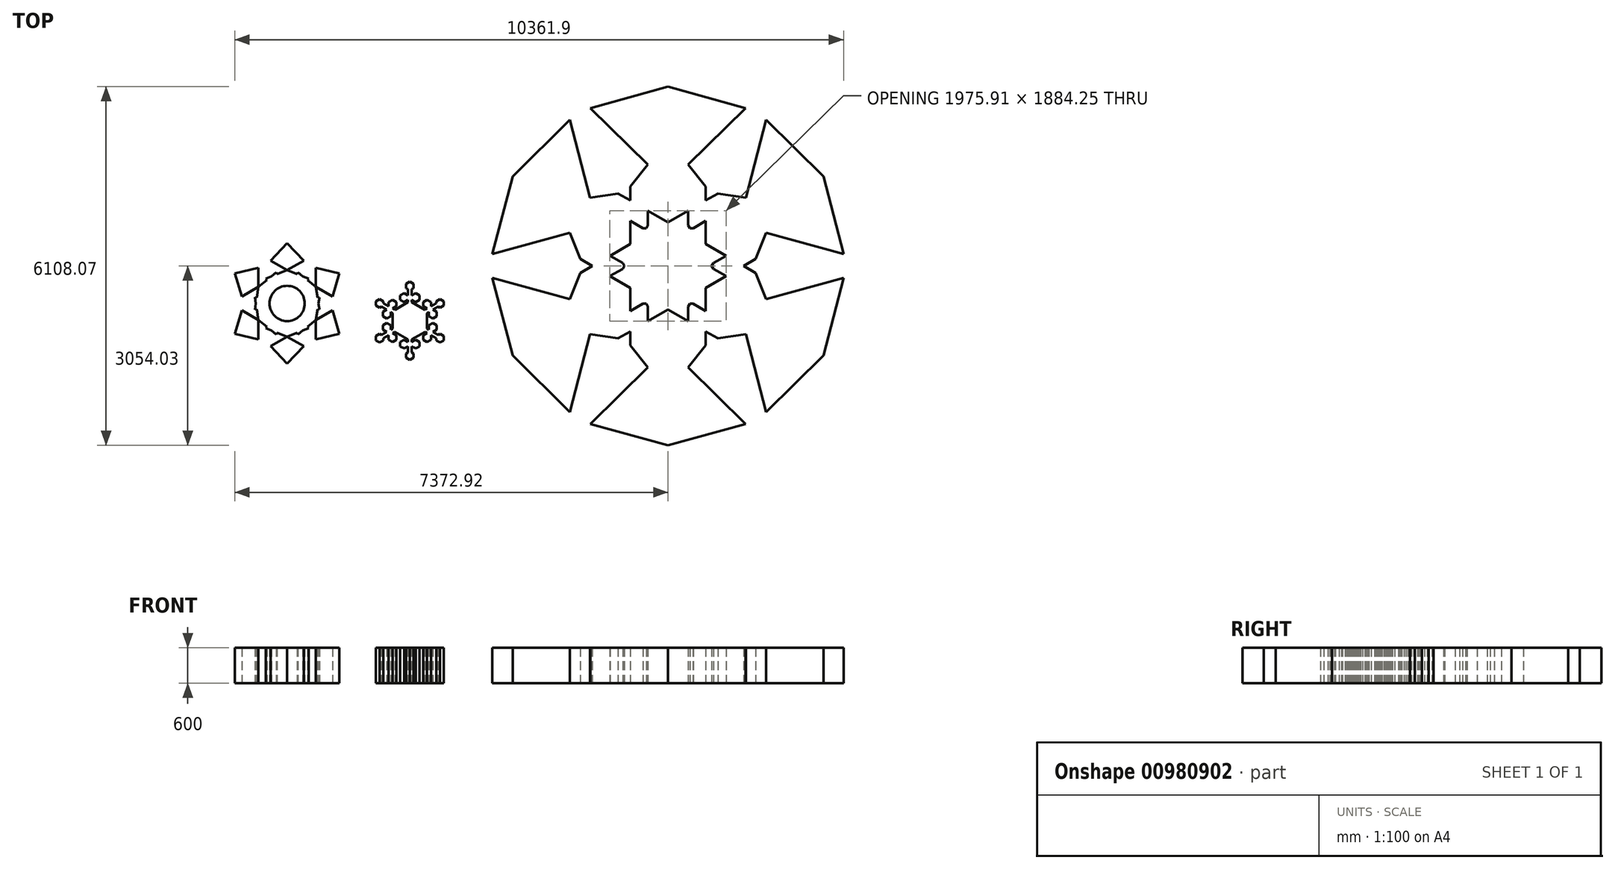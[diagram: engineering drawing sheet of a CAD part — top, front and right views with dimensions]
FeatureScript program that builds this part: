
annotation { "Feature Type Name" : "Feature", "Feature Type Description" : "" }
export const myFeature = defineFeature(function(context is Context, id is Id, definition is map)
    precondition{}
    {
        {
            var Q0;
            Q0=qCreatedBy(makeId("Top.planeOp"),FACE);
            var sketch = newSketch(context, id + "F0", { "sketchPlane" : qUnion([Q0])});
            skLineSegment(sketch, "E0", {"start": v(525.43, 83.54) * mm, "end": v(525.43, -246.83) * mm});
            skCircle(sketch, "E1.cCircle", {"center": v(525.43, 251.11) * mm, "radius": 145.12 * mm, "construction": true});
            skLineSegment(sketch, "E1.0", {"start": v(670.55, 167.33) * mm, "end": v(525.43, 83.54) * mm});
            skLineSegment(sketch, "E1.1", {"start": v(525.43, 83.54) * mm, "end": v(380.31, 167.33) * mm});
            skLineSegment(sketch, "E1.2", {"start": v(380.31, 167.33) * mm, "end": v(380.31, 334.9) * mm});
            skLineSegment(sketch, "E1.3", {"start": v(380.31, 334.9) * mm, "end": v(525.43, 418.68) * mm});
            skLineSegment(sketch, "E1.4", {"start": v(525.43, 418.68) * mm, "end": v(670.55, 334.9) * mm});
            skLineSegment(sketch, "E1.5", {"start": v(670.55, 334.9) * mm, "end": v(670.55, 167.33) * mm});
            skPoint(sketch, "E1.0.midPoint", {"position": v(598, 125.43) * mm});
            skCircle(sketch, "E2.cCircle", {"center": v(525.43, -173.92) * mm, "radius": 63.14 * mm, "construction": true});
            skLineSegment(sketch, "E2.0", {"start": v(525.43, -246.83) * mm, "end": v(462.3, -210.38) * mm});
            skLineSegment(sketch, "E2.1", {"start": v(462.3, -210.38) * mm, "end": v(462.3, -137.47) * mm});
            skLineSegment(sketch, "E2.2", {"start": v(462.3, -137.47) * mm, "end": v(525.43, -101.01) * mm});
            skLineSegment(sketch, "E2.3", {"start": v(525.43, -101.01) * mm, "end": v(588.57, -137.47) * mm});
            skLineSegment(sketch, "E2.4", {"start": v(588.57, -137.47) * mm, "end": v(588.57, -210.38) * mm});
            skLineSegment(sketch, "E2.5", {"start": v(588.57, -210.38) * mm, "end": v(525.43, -246.83) * mm});
            skPoint(sketch, "E2.0.midPoint", {"position": v(493.86, -228.6) * mm});
            skLineSegment(sketch, "E3", {"start": v(492.43, 102.6) * mm, "end": v(492.43, -120.07) * mm});
            skLineSegment(sketch, "E4.MirrorCS", {"start": v(558.43, 102.6) * mm, "end": v(558.43, -120.07) * mm});
            skCircle(sketch, "E5.cCircle", {"center": v(426.9, 22.57) * mm, "radius": 65.53 * mm, "construction": true});
            skLineSegment(sketch, "E5.0", {"start": v(492.43, -15.27) * mm, "end": v(426.9, -53.1) * mm});
            skLineSegment(sketch, "E5.1", {"start": v(426.9, -53.1) * mm, "end": v(361.36, -15.27) * mm});
            skLineSegment(sketch, "E5.2", {"start": v(361.36, -15.27) * mm, "end": v(361.36, 60.4) * mm});
            skLineSegment(sketch, "E5.3", {"start": v(361.36, 60.4) * mm, "end": v(426.9, 98.24) * mm});
            skLineSegment(sketch, "E5.4", {"start": v(426.9, 98.24) * mm, "end": v(492.43, 60.4) * mm});
            skLineSegment(sketch, "E5.5", {"start": v(492.43, 60.4) * mm, "end": v(492.43, -15.27) * mm});
            skPoint(sketch, "E5.0.midPoint", {"position": v(459.67, -34.18) * mm});
            skLineSegment(sketch, "E6.MirrorCS", {"start": v(689.5, -15.27) * mm, "end": v(689.5, 60.4) * mm});
            skLineSegment(sketch, "E7.MirrorCS", {"start": v(689.5, 60.4) * mm, "end": v(623.97, 98.24) * mm});
            skLineSegment(sketch, "E8.MirrorCS", {"start": v(623.97, 98.24) * mm, "end": v(558.43, 60.4) * mm});
            skLineSegment(sketch, "E9.MirrorCS", {"start": v(558.43, -15.27) * mm, "end": v(623.97, -53.1) * mm});
            skLineSegment(sketch, "E10.MirrorCS", {"start": v(623.97, -53.1) * mm, "end": v(689.5, -15.27) * mm});
            skLineSegment(sketch, "E11.1.0", {"start": v(815.68, 251.11) * mm, "end": v(1101.79, 85.92) * mm});
            skLineSegment(sketch, "E11.1.1", {"start": v(815.68, 289.22) * mm, "end": v(1008.5, 177.89) * mm});
            skLineSegment(sketch, "E11.1.2", {"start": v(815.68, 418.68) * mm, "end": v(815.68, 251.11) * mm});
            skLineSegment(sketch, "E11.1.3", {"start": v(525.43, 418.68) * mm, "end": v(670.55, 502.47) * mm});
            skCircle(sketch, "E11.1.4", {"center": v(670.55, 334.9) * mm, "radius": 145.12 * mm, "construction": true});
            skLineSegment(sketch, "E11.1.5", {"start": v(917.74, 230.29) * mm, "end": v(983.28, 268.12) * mm});
            skPoint(sketch, "E11.1.6", {"position": v(815.68, 334.9) * mm});
            skLineSegment(sketch, "E11.1.7", {"start": v(983.28, 343.8) * mm, "end": v(917.74, 381.63) * mm});
            skLineSegment(sketch, "E11.1.8", {"start": v(917.74, 381.63) * mm, "end": v(852.2, 343.8) * mm});
            skLineSegment(sketch, "E11.1.9", {"start": v(670.55, 167.33) * mm, "end": v(525.43, 251.11) * mm});
            skPoint(sketch, "E11.1.10", {"position": v(884.74, 135.3) * mm});
            skLineSegment(sketch, "E11.1.11", {"start": v(815.68, 251.11) * mm, "end": v(670.55, 167.33) * mm});
            skCircle(sketch, "E11.1.12", {"center": v(1038.65, 122.38) * mm, "radius": 63.14 * mm, "construction": true});
            skLineSegment(sketch, "E11.1.13", {"start": v(983.28, 268.12) * mm, "end": v(983.28, 343.8) * mm});
            skLineSegment(sketch, "E11.1.14", {"start": v(670.55, 502.47) * mm, "end": v(815.68, 418.68) * mm});
            skCircle(sketch, "E11.1.15", {"center": v(819.2, 135.3) * mm, "radius": 65.53 * mm, "construction": true});
            skPoint(sketch, "E11.1.16", {"position": v(1070.22, 67.7) * mm});
            skLineSegment(sketch, "E11.1.17", {"start": v(525.43, 251.11) * mm, "end": v(525.43, 418.68) * mm});
            skLineSegment(sketch, "E11.1.18", {"start": v(782.68, 232.06) * mm, "end": v(975.5, 120.73) * mm});
            skLineSegment(sketch, "E11.1.19", {"start": v(852.2, 343.8) * mm, "end": v(852.2, 268.12) * mm});
            skLineSegment(sketch, "E11.1.20", {"start": v(1038.65, 195.3) * mm, "end": v(1101.79, 158.84) * mm});
            skLineSegment(sketch, "E11.1.21", {"start": v(819.2, 210.97) * mm, "end": v(884.74, 173.13) * mm});
            skLineSegment(sketch, "E11.1.22", {"start": v(1038.65, 49.47) * mm, "end": v(975.5, 85.92) * mm});
            skLineSegment(sketch, "E11.1.23", {"start": v(1101.79, 158.84) * mm, "end": v(1101.79, 85.92) * mm});
            skLineSegment(sketch, "E11.1.24", {"start": v(975.5, 85.92) * mm, "end": v(975.5, 158.84) * mm});
            skLineSegment(sketch, "E11.1.25", {"start": v(884.74, 97.46) * mm, "end": v(819.2, 59.62) * mm});
            skLineSegment(sketch, "E11.1.26", {"start": v(975.5, 158.84) * mm, "end": v(1038.65, 195.3) * mm});
            skLineSegment(sketch, "E11.1.27", {"start": v(753.67, 173.13) * mm, "end": v(819.2, 210.97) * mm});
            skLineSegment(sketch, "E11.1.28", {"start": v(884.74, 173.13) * mm, "end": v(884.74, 97.46) * mm});
            skLineSegment(sketch, "E11.1.29", {"start": v(1101.79, 85.92) * mm, "end": v(1038.65, 49.47) * mm});
            skLineSegment(sketch, "E11.1.30", {"start": v(753.67, 97.46) * mm, "end": v(753.67, 173.13) * mm});
            skLineSegment(sketch, "E11.1.31", {"start": v(819.2, 59.62) * mm, "end": v(753.67, 97.46) * mm});
            skLineSegment(sketch, "E11.2.0", {"start": v(815.68, 586.26) * mm, "end": v(1101.79, 751.44) * mm});
            skLineSegment(sketch, "E11.2.1", {"start": v(782.68, 605.3) * mm, "end": v(975.5, 716.64) * mm});
            skLineSegment(sketch, "E11.2.2", {"start": v(670.55, 670.04) * mm, "end": v(815.68, 586.26) * mm});
            skLineSegment(sketch, "E11.2.3", {"start": v(525.43, 418.68) * mm, "end": v(525.43, 586.26) * mm});
            skCircle(sketch, "E11.2.4", {"center": v(670.55, 502.47) * mm, "radius": 145.12 * mm, "construction": true});
            skLineSegment(sketch, "E11.2.5", {"start": v(884.74, 664.24) * mm, "end": v(884.74, 739.9) * mm});
            skPoint(sketch, "E11.2.6", {"position": v(743.11, 628.15) * mm});
            skLineSegment(sketch, "E11.2.7", {"start": v(819.2, 777.75) * mm, "end": v(753.67, 739.9) * mm});
            skLineSegment(sketch, "E11.2.8", {"start": v(753.67, 739.9) * mm, "end": v(753.67, 664.24) * mm});
            skLineSegment(sketch, "E11.2.9", {"start": v(815.68, 418.68) * mm, "end": v(670.55, 334.9) * mm});
            skPoint(sketch, "E11.2.10", {"position": v(950.51, 588.16) * mm});
            skLineSegment(sketch, "E11.2.11", {"start": v(815.68, 586.26) * mm, "end": v(815.68, 418.68) * mm});
            skCircle(sketch, "E11.2.12", {"center": v(1038.65, 714.99) * mm, "radius": 63.14 * mm, "construction": true});
            skLineSegment(sketch, "E11.2.13", {"start": v(884.74, 739.9) * mm, "end": v(819.2, 777.75) * mm});
            skLineSegment(sketch, "E11.2.14", {"start": v(525.43, 586.26) * mm, "end": v(670.55, 670.04) * mm});
            skCircle(sketch, "E11.2.15", {"center": v(917.74, 531.4) * mm, "radius": 65.53 * mm, "construction": true});
            skPoint(sketch, "E11.2.16", {"position": v(1101.79, 714.99) * mm});
            skLineSegment(sketch, "E11.2.17", {"start": v(670.55, 334.9) * mm, "end": v(525.43, 418.68) * mm});
            skLineSegment(sketch, "E11.2.18", {"start": v(815.68, 548.15) * mm, "end": v(1008.5, 659.48) * mm});
            skLineSegment(sketch, "E11.2.19", {"start": v(753.67, 664.24) * mm, "end": v(819.2, 626.4) * mm});
            skLineSegment(sketch, "E11.2.20", {"start": v(975.5, 751.44) * mm, "end": v(1038.65, 787.9) * mm});
            skLineSegment(sketch, "E11.2.21", {"start": v(852.2, 569.24) * mm, "end": v(917.74, 607.08) * mm});
            skLineSegment(sketch, "E11.2.22", {"start": v(1101.79, 678.53) * mm, "end": v(1038.65, 642.08) * mm});
            skLineSegment(sketch, "E11.2.23", {"start": v(1038.65, 787.9) * mm, "end": v(1101.79, 751.44) * mm});
            skLineSegment(sketch, "E11.2.24", {"start": v(1038.65, 642.08) * mm, "end": v(975.5, 678.53) * mm});
            skLineSegment(sketch, "E11.2.25", {"start": v(983.28, 569.24) * mm, "end": v(983.28, 493.57) * mm});
            skLineSegment(sketch, "E11.2.26", {"start": v(975.5, 678.53) * mm, "end": v(975.5, 751.44) * mm});
            skLineSegment(sketch, "E11.2.27", {"start": v(852.2, 493.57) * mm, "end": v(852.2, 569.24) * mm});
            skLineSegment(sketch, "E11.2.28", {"start": v(917.74, 607.08) * mm, "end": v(983.28, 569.24) * mm});
            skLineSegment(sketch, "E11.2.29", {"start": v(1101.79, 751.44) * mm, "end": v(1101.79, 678.53) * mm});
            skLineSegment(sketch, "E11.2.30", {"start": v(917.74, 455.73) * mm, "end": v(852.2, 493.57) * mm});
            skLineSegment(sketch, "E11.2.31", {"start": v(983.28, 493.57) * mm, "end": v(917.74, 455.73) * mm});
            skLineSegment(sketch, "E11.3.0", {"start": v(525.43, 753.83) * mm, "end": v(525.43, 1084.2) * mm});
            skLineSegment(sketch, "E11.3.1", {"start": v(492.43, 734.78) * mm, "end": v(492.43, 957.43) * mm});
            skLineSegment(sketch, "E11.3.2", {"start": v(380.31, 670.04) * mm, "end": v(525.43, 753.83) * mm});
            skLineSegment(sketch, "E11.3.3", {"start": v(525.43, 418.68) * mm, "end": v(380.31, 502.47) * mm});
            skCircle(sketch, "E11.3.4", {"center": v(525.43, 586.26) * mm, "radius": 145.12 * mm, "construction": true});
            skLineSegment(sketch, "E11.3.5", {"start": v(492.43, 852.63) * mm, "end": v(426.9, 890.47) * mm});
            skPoint(sketch, "E11.3.6", {"position": v(452.87, 711.93) * mm});
            skLineSegment(sketch, "E11.3.7", {"start": v(361.36, 852.63) * mm, "end": v(361.36, 776.96) * mm});
            skLineSegment(sketch, "E11.3.8", {"start": v(361.36, 776.96) * mm, "end": v(426.9, 739.12) * mm});
            skLineSegment(sketch, "E11.3.9", {"start": v(670.55, 670.04) * mm, "end": v(670.55, 502.47) * mm});
            skPoint(sketch, "E11.3.10", {"position": v(591.2, 871.55) * mm});
            skLineSegment(sketch, "E11.3.11", {"start": v(525.43, 753.83) * mm, "end": v(670.55, 670.04) * mm});
            skCircle(sketch, "E11.3.12", {"center": v(525.43, 1011.3) * mm, "radius": 63.14 * mm, "construction": true});
            skLineSegment(sketch, "E11.3.13", {"start": v(426.9, 890.47) * mm, "end": v(361.36, 852.63) * mm});
            skLineSegment(sketch, "E11.3.14", {"start": v(380.31, 502.47) * mm, "end": v(380.31, 670.04) * mm});
            skCircle(sketch, "E11.3.15", {"center": v(623.97, 814.8) * mm, "radius": 65.53 * mm, "construction": true});
            skPoint(sketch, "E11.3.16", {"position": v(557, 1065.97) * mm});
            skLineSegment(sketch, "E11.3.17", {"start": v(670.55, 502.47) * mm, "end": v(525.43, 418.68) * mm});
            skLineSegment(sketch, "E11.3.18", {"start": v(558.43, 734.78) * mm, "end": v(558.43, 957.43) * mm});
            skLineSegment(sketch, "E11.3.19", {"start": v(426.9, 739.12) * mm, "end": v(492.43, 776.96) * mm});
            skLineSegment(sketch, "E11.3.20", {"start": v(462.3, 974.84) * mm, "end": v(462.3, 1047.75) * mm});
            skLineSegment(sketch, "E11.3.21", {"start": v(558.43, 776.96) * mm, "end": v(558.43, 852.63) * mm});
            skLineSegment(sketch, "E11.3.22", {"start": v(588.57, 1047.75) * mm, "end": v(588.57, 974.84) * mm});
            skLineSegment(sketch, "E11.3.23", {"start": v(462.3, 1047.75) * mm, "end": v(525.43, 1084.2) * mm});
            skLineSegment(sketch, "E11.3.24", {"start": v(588.57, 974.84) * mm, "end": v(525.43, 938.38) * mm});
            skLineSegment(sketch, "E11.3.25", {"start": v(623.97, 890.47) * mm, "end": v(689.5, 852.63) * mm});
            skLineSegment(sketch, "E11.3.26", {"start": v(525.43, 938.38) * mm, "end": v(462.3, 974.84) * mm});
            skLineSegment(sketch, "E11.3.27", {"start": v(623.97, 739.12) * mm, "end": v(558.43, 776.96) * mm});
            skLineSegment(sketch, "E11.3.28", {"start": v(558.43, 852.63) * mm, "end": v(623.97, 890.47) * mm});
            skLineSegment(sketch, "E11.3.29", {"start": v(525.43, 1084.2) * mm, "end": v(588.57, 1047.75) * mm});
            skLineSegment(sketch, "E11.3.30", {"start": v(689.5, 776.96) * mm, "end": v(623.97, 739.12) * mm});
            skLineSegment(sketch, "E11.3.31", {"start": v(689.5, 852.63) * mm, "end": v(689.5, 776.96) * mm});
            skLineSegment(sketch, "E11.4.0", {"start": v(235.19, 586.26) * mm, "end": v(-50.92, 751.44) * mm});
            skLineSegment(sketch, "E11.4.1", {"start": v(235.19, 548.15) * mm, "end": v(42.36, 659.48) * mm});
            skLineSegment(sketch, "E11.4.2", {"start": v(235.19, 418.68) * mm, "end": v(235.19, 586.26) * mm});
            skLineSegment(sketch, "E11.4.3", {"start": v(525.43, 418.68) * mm, "end": v(380.31, 334.9) * mm});
            skCircle(sketch, "E11.4.4", {"center": v(380.31, 502.47) * mm, "radius": 145.12 * mm, "construction": true});
            skLineSegment(sketch, "E11.4.5", {"start": v(133.12, 607.08) * mm, "end": v(67.59, 569.24) * mm});
            skPoint(sketch, "E11.4.6", {"position": v(235.19, 502.47) * mm});
            skLineSegment(sketch, "E11.4.7", {"start": v(67.59, 493.57) * mm, "end": v(133.12, 455.73) * mm});
            skLineSegment(sketch, "E11.4.8", {"start": v(133.12, 455.73) * mm, "end": v(198.66, 493.57) * mm});
            skLineSegment(sketch, "E11.4.9", {"start": v(380.31, 670.04) * mm, "end": v(525.43, 586.26) * mm});
            skPoint(sketch, "E11.4.10", {"position": v(166.12, 702.07) * mm});
            skLineSegment(sketch, "E11.4.11", {"start": v(235.19, 586.26) * mm, "end": v(380.31, 670.04) * mm});
            skCircle(sketch, "E11.4.12", {"center": v(12.22, 714.99) * mm, "radius": 63.14 * mm, "construction": true});
            skLineSegment(sketch, "E11.4.13", {"start": v(67.59, 569.24) * mm, "end": v(67.59, 493.57) * mm});
            skLineSegment(sketch, "E11.4.14", {"start": v(380.31, 334.9) * mm, "end": v(235.19, 418.68) * mm});
            skCircle(sketch, "E11.4.15", {"center": v(231.66, 702.07) * mm, "radius": 65.53 * mm, "construction": true});
            skPoint(sketch, "E11.4.16", {"position": v(-19.35, 769.67) * mm});
            skLineSegment(sketch, "E11.4.17", {"start": v(525.43, 586.26) * mm, "end": v(525.43, 418.68) * mm});
            skLineSegment(sketch, "E11.4.18", {"start": v(268.19, 605.3) * mm, "end": v(75.36, 716.64) * mm});
            skLineSegment(sketch, "E11.4.19", {"start": v(198.66, 493.57) * mm, "end": v(198.66, 569.24) * mm});
            skLineSegment(sketch, "E11.4.20", {"start": v(12.22, 642.08) * mm, "end": v(-50.92, 678.53) * mm});
            skLineSegment(sketch, "E11.4.21", {"start": v(231.66, 626.4) * mm, "end": v(166.12, 664.24) * mm});
            skLineSegment(sketch, "E11.4.22", {"start": v(12.22, 787.9) * mm, "end": v(75.36, 751.44) * mm});
            skLineSegment(sketch, "E11.4.23", {"start": v(-50.92, 678.53) * mm, "end": v(-50.92, 751.44) * mm});
            skLineSegment(sketch, "E11.4.24", {"start": v(75.36, 751.44) * mm, "end": v(75.36, 678.53) * mm});
            skLineSegment(sketch, "E11.4.25", {"start": v(166.12, 739.9) * mm, "end": v(231.66, 777.75) * mm});
            skLineSegment(sketch, "E11.4.26", {"start": v(75.36, 678.53) * mm, "end": v(12.22, 642.08) * mm});
            skLineSegment(sketch, "E11.4.27", {"start": v(297.2, 664.24) * mm, "end": v(231.66, 626.4) * mm});
            skLineSegment(sketch, "E11.4.28", {"start": v(166.12, 664.24) * mm, "end": v(166.12, 739.9) * mm});
            skLineSegment(sketch, "E11.4.29", {"start": v(-50.92, 751.44) * mm, "end": v(12.22, 787.9) * mm});
            skLineSegment(sketch, "E11.4.30", {"start": v(297.2, 739.9) * mm, "end": v(297.2, 664.24) * mm});
            skLineSegment(sketch, "E11.4.31", {"start": v(231.66, 777.75) * mm, "end": v(297.2, 739.9) * mm});
            skLineSegment(sketch, "E11.5.0", {"start": v(235.19, 251.11) * mm, "end": v(-50.92, 85.92) * mm});
            skLineSegment(sketch, "E11.5.1", {"start": v(268.19, 232.06) * mm, "end": v(75.36, 120.73) * mm});
            skLineSegment(sketch, "E11.5.2", {"start": v(380.31, 167.33) * mm, "end": v(235.19, 251.11) * mm});
            skLineSegment(sketch, "E11.5.3", {"start": v(525.43, 418.68) * mm, "end": v(525.43, 251.11) * mm});
            skCircle(sketch, "E11.5.4", {"center": v(380.31, 334.9) * mm, "radius": 145.12 * mm, "construction": true});
            skLineSegment(sketch, "E11.5.5", {"start": v(166.12, 173.13) * mm, "end": v(166.12, 97.46) * mm});
            skPoint(sketch, "E11.5.6", {"position": v(307.75, 209.22) * mm});
            skLineSegment(sketch, "E11.5.7", {"start": v(231.66, 59.62) * mm, "end": v(297.2, 97.46) * mm});
            skLineSegment(sketch, "E11.5.8", {"start": v(297.2, 97.46) * mm, "end": v(297.2, 173.13) * mm});
            skLineSegment(sketch, "E11.5.9", {"start": v(235.19, 418.68) * mm, "end": v(380.31, 502.47) * mm});
            skPoint(sketch, "E11.5.10", {"position": v(100.35, 249.2) * mm});
            skLineSegment(sketch, "E11.5.11", {"start": v(235.19, 251.11) * mm, "end": v(235.19, 418.68) * mm});
            skCircle(sketch, "E11.5.12", {"center": v(12.22, 122.38) * mm, "radius": 63.14 * mm, "construction": true});
            skLineSegment(sketch, "E11.5.13", {"start": v(166.12, 97.46) * mm, "end": v(231.66, 59.62) * mm});
            skLineSegment(sketch, "E11.5.14", {"start": v(525.43, 251.11) * mm, "end": v(380.31, 167.33) * mm});
            skCircle(sketch, "E11.5.15", {"center": v(133.12, 305.96) * mm, "radius": 65.53 * mm, "construction": true});
            skPoint(sketch, "E11.5.16", {"position": v(-50.92, 122.38) * mm});
            skLineSegment(sketch, "E11.5.17", {"start": v(380.31, 502.47) * mm, "end": v(525.43, 418.68) * mm});
            skLineSegment(sketch, "E11.5.18", {"start": v(235.19, 289.22) * mm, "end": v(42.36, 177.89) * mm});
            skLineSegment(sketch, "E11.5.19", {"start": v(297.2, 173.13) * mm, "end": v(231.66, 210.97) * mm});
            skLineSegment(sketch, "E11.5.20", {"start": v(75.36, 85.92) * mm, "end": v(12.22, 49.47) * mm});
            skLineSegment(sketch, "E11.5.21", {"start": v(198.66, 268.12) * mm, "end": v(133.12, 230.29) * mm});
            skLineSegment(sketch, "E11.5.22", {"start": v(-50.92, 158.84) * mm, "end": v(12.22, 195.3) * mm});
            skLineSegment(sketch, "E11.5.23", {"start": v(12.22, 49.47) * mm, "end": v(-50.92, 85.92) * mm});
            skLineSegment(sketch, "E11.5.24", {"start": v(12.22, 195.3) * mm, "end": v(75.36, 158.84) * mm});
            skLineSegment(sketch, "E11.5.25", {"start": v(67.59, 268.12) * mm, "end": v(67.59, 343.8) * mm});
            skLineSegment(sketch, "E11.5.26", {"start": v(75.36, 158.84) * mm, "end": v(75.36, 85.92) * mm});
            skLineSegment(sketch, "E11.5.27", {"start": v(198.66, 343.8) * mm, "end": v(198.66, 268.12) * mm});
            skLineSegment(sketch, "E11.5.28", {"start": v(133.12, 230.29) * mm, "end": v(67.59, 268.12) * mm});
            skLineSegment(sketch, "E11.5.29", {"start": v(-50.92, 85.92) * mm, "end": v(-50.92, 158.84) * mm});
            skLineSegment(sketch, "E11.5.30", {"start": v(133.12, 381.63) * mm, "end": v(198.66, 343.8) * mm});
            skLineSegment(sketch, "E11.5.31", {"start": v(67.59, 343.8) * mm, "end": v(133.12, 381.63) * mm});
            skPoint(sketch, "E11.center", {"position": v(525.43, 418.68) * mm});
            skCircle(sketch, "E12", {"center": v(-1562.58, 714.6) * mm, "radius": 299.9 * mm, "construction": true});
            skLineSegment(sketch, "E13", {"start": v(-1562.58, 714.6) * mm, "end": v(-1562.58, 1742.85) * mm});
            skLineSegment(sketch, "E14", {"start": v(-1562.58, 1742.85) * mm, "end": v(-1846.13, 1442.94) * mm});
            skLineSegment(sketch, "E15", {"start": v(-1846.13, 1442.94) * mm, "end": v(-1562.58, 1281.45) * mm});
            skLineSegment(sketch, "E16", {"start": v(-1562.58, 1281.45) * mm, "end": v(-1928.52, 1136.44) * mm});
            skLineSegment(sketch, "E17", {"start": v(-1928.52, 1136.44) * mm, "end": v(-1562.58, 714.6) * mm});
            skLineSegment(sketch, "E18.MirrorCS", {"start": v(-1562.58, 1742.85) * mm, "end": v(-1279.03, 1442.94) * mm});
            skLineSegment(sketch, "E19.MirrorCS", {"start": v(-1279.03, 1442.94) * mm, "end": v(-1562.58, 1281.45) * mm});
            skLineSegment(sketch, "E20.MirrorCS", {"start": v(-1562.58, 1281.45) * mm, "end": v(-1196.63, 1136.44) * mm});
            skLineSegment(sketch, "E21.MirrorCS", {"start": v(-1196.63, 1136.44) * mm, "end": v(-1562.58, 714.6) * mm});
            skLineSegment(sketch, "E22.1.0", {"start": v(-2335.12, 833.21) * mm, "end": v(-2053.5, 998.03) * mm});
            skLineSegment(sketch, "E22.1.1", {"start": v(-2110.88, 608.6) * mm, "end": v(-1562.58, 714.6) * mm});
            skLineSegment(sketch, "E22.1.2", {"start": v(-1744.94, 1242.44) * mm, "end": v(-1562.58, 714.6) * mm});
            skCircle(sketch, "E22.1.3", {"center": v(-1562.58, 714.6) * mm, "radius": 299.9 * mm});
            skLineSegment(sketch, "E22.1.4", {"start": v(-2453.07, 1228.72) * mm, "end": v(-2335.12, 833.21) * mm});
            skLineSegment(sketch, "E22.1.5", {"start": v(-2051.57, 1324.33) * mm, "end": v(-2053.5, 998.03) * mm});
            skLineSegment(sketch, "E22.1.6", {"start": v(-2453.07, 1228.72) * mm, "end": v(-2051.57, 1324.33) * mm});
            skLineSegment(sketch, "E22.1.7", {"start": v(-1562.58, 714.6) * mm, "end": v(-2453.07, 1228.72) * mm});
            skLineSegment(sketch, "E22.1.8", {"start": v(-2053.5, 998.03) * mm, "end": v(-1744.94, 1242.44) * mm});
            skLineSegment(sketch, "E22.1.9", {"start": v(-2053.5, 998.03) * mm, "end": v(-2110.88, 608.6) * mm});
            skLineSegment(sketch, "E22.2.0", {"start": v(-2051.57, 104.87) * mm, "end": v(-2053.5, 431.17) * mm});
            skLineSegment(sketch, "E22.2.1", {"start": v(-1744.94, 186.76) * mm, "end": v(-1562.58, 714.6) * mm});
            skLineSegment(sketch, "E22.2.2", {"start": v(-2110.88, 820.6) * mm, "end": v(-1562.58, 714.6) * mm});
            skCircle(sketch, "E22.2.3", {"center": v(-1562.58, 714.6) * mm, "radius": 299.9 * mm});
            skLineSegment(sketch, "E22.2.4", {"start": v(-2453.07, 200.47) * mm, "end": v(-2051.57, 104.87) * mm});
            skLineSegment(sketch, "E22.2.5", {"start": v(-2335.12, 595.98) * mm, "end": v(-2053.5, 431.17) * mm});
            skLineSegment(sketch, "E22.2.6", {"start": v(-2453.07, 200.47) * mm, "end": v(-2335.12, 595.98) * mm});
            skLineSegment(sketch, "E22.2.7", {"start": v(-1562.58, 714.6) * mm, "end": v(-2453.07, 200.47) * mm});
            skLineSegment(sketch, "E22.2.8", {"start": v(-2053.5, 431.17) * mm, "end": v(-2110.88, 820.6) * mm});
            skLineSegment(sketch, "E22.2.9", {"start": v(-2053.5, 431.17) * mm, "end": v(-1744.94, 186.76) * mm});
            skLineSegment(sketch, "E22.3.0", {"start": v(-1279.03, -13.75) * mm, "end": v(-1562.58, 147.74) * mm});
            skLineSegment(sketch, "E22.3.1", {"start": v(-1196.63, 292.75) * mm, "end": v(-1562.58, 714.6) * mm});
            skLineSegment(sketch, "E22.3.2", {"start": v(-1928.52, 292.75) * mm, "end": v(-1562.58, 714.6) * mm});
            skCircle(sketch, "E22.3.3", {"center": v(-1562.58, 714.6) * mm, "radius": 299.9 * mm});
            skLineSegment(sketch, "E22.3.4", {"start": v(-1562.58, -313.65) * mm, "end": v(-1279.03, -13.75) * mm});
            skLineSegment(sketch, "E22.3.5", {"start": v(-1846.13, -13.75) * mm, "end": v(-1562.58, 147.74) * mm});
            skLineSegment(sketch, "E22.3.6", {"start": v(-1562.58, -313.65) * mm, "end": v(-1846.13, -13.75) * mm});
            skLineSegment(sketch, "E22.3.7", {"start": v(-1562.58, 714.6) * mm, "end": v(-1562.58, -313.65) * mm});
            skLineSegment(sketch, "E22.3.8", {"start": v(-1562.58, 147.74) * mm, "end": v(-1928.52, 292.75) * mm});
            skLineSegment(sketch, "E22.3.9", {"start": v(-1562.58, 147.74) * mm, "end": v(-1196.63, 292.75) * mm});
            skLineSegment(sketch, "E22.4.0", {"start": v(-790.04, 595.98) * mm, "end": v(-1071.67, 431.17) * mm});
            skLineSegment(sketch, "E22.4.1", {"start": v(-1014.28, 820.6) * mm, "end": v(-1562.58, 714.6) * mm});
            skLineSegment(sketch, "E22.4.2", {"start": v(-1380.22, 186.76) * mm, "end": v(-1562.58, 714.6) * mm});
            skCircle(sketch, "E22.4.3", {"center": v(-1562.58, 714.6) * mm, "radius": 299.9 * mm});
            skLineSegment(sketch, "E22.4.4", {"start": v(-672.09, 200.47) * mm, "end": v(-790.04, 595.98) * mm});
            skLineSegment(sketch, "E22.4.5", {"start": v(-1073.59, 104.87) * mm, "end": v(-1071.67, 431.17) * mm});
            skLineSegment(sketch, "E22.4.6", {"start": v(-672.09, 200.47) * mm, "end": v(-1073.59, 104.87) * mm});
            skLineSegment(sketch, "E22.4.7", {"start": v(-1562.58, 714.6) * mm, "end": v(-672.09, 200.47) * mm});
            skLineSegment(sketch, "E22.4.8", {"start": v(-1071.67, 431.17) * mm, "end": v(-1380.22, 186.76) * mm});
            skLineSegment(sketch, "E22.4.9", {"start": v(-1071.67, 431.17) * mm, "end": v(-1014.28, 820.6) * mm});
            skLineSegment(sketch, "E22.5.0", {"start": v(-1073.59, 1324.33) * mm, "end": v(-1071.67, 998.03) * mm});
            skLineSegment(sketch, "E22.5.1", {"start": v(-1380.22, 1242.44) * mm, "end": v(-1562.58, 714.6) * mm});
            skLineSegment(sketch, "E22.5.2", {"start": v(-1014.28, 608.6) * mm, "end": v(-1562.58, 714.6) * mm});
            skCircle(sketch, "E22.5.3", {"center": v(-1562.58, 714.6) * mm, "radius": 299.9 * mm});
            skLineSegment(sketch, "E22.5.4", {"start": v(-672.09, 1228.72) * mm, "end": v(-1073.59, 1324.33) * mm});
            skLineSegment(sketch, "E22.5.5", {"start": v(-790.04, 833.21) * mm, "end": v(-1071.67, 998.03) * mm});
            skLineSegment(sketch, "E22.5.6", {"start": v(-672.09, 1228.72) * mm, "end": v(-790.04, 833.21) * mm});
            skLineSegment(sketch, "E22.5.7", {"start": v(-1562.58, 714.6) * mm, "end": v(-672.09, 1228.72) * mm});
            skLineSegment(sketch, "E22.5.8", {"start": v(-1071.67, 998.03) * mm, "end": v(-1014.28, 608.6) * mm});
            skLineSegment(sketch, "E22.5.9", {"start": v(-1071.67, 998.03) * mm, "end": v(-1380.22, 1242.44) * mm});
            skLineSegment(sketch, "E23", {"start": v(4919.85, 1353.05) * mm, "end": v(4919.85, -1700.98) * mm});
            skCircle(sketch, "E24.cCircle", {"center": v(4919.85, 1353.05) * mm, "radius": 643.86 * mm, "construction": true});
            skLineSegment(sketch, "E24.0", {"start": v(5563.7, 1996.9) * mm, "end": v(5563.7, 709.2) * mm});
            skLineSegment(sketch, "E24.1", {"start": v(5563.7, 709.2) * mm, "end": v(4276, 709.2) * mm});
            skLineSegment(sketch, "E24.2", {"start": v(4276, 709.2) * mm, "end": v(4276, 1996.9) * mm});
            skLineSegment(sketch, "E24.3", {"start": v(4276, 1996.9) * mm, "end": v(5563.7, 1996.9) * mm});
            skPoint(sketch, "E24.0.midPoint", {"position": v(5563.7, 1353.05) * mm});
            skLineSegment(sketch, "E25", {"start": v(4575.75, 808.86) * mm, "end": v(4575.75, -375.17) * mm});
            skLineSegment(sketch, "E26", {"start": v(5263.15, 808.36) * mm, "end": v(5263.15, -375.67) * mm});
            skCircle(sketch, "E27.cCircle", {"center": v(4365.07, -1137.4) * mm, "radius": 395.4 * mm, "construction": true});
            skLineSegment(sketch, "E27.0", {"start": v(4919.85, -1700.98) * mm, "end": v(3599.6, -1336.08) * mm});
            skLineSegment(sketch, "E27.1", {"start": v(3599.6, -1336.08) * mm, "end": v(4575.75, -375.17) * mm});
            skLineSegment(sketch, "E27.2", {"start": v(4575.75, -375.17) * mm, "end": v(4919.85, -1700.98) * mm});
            skPoint(sketch, "E27.0.midPoint", {"position": v(4259.73, -1518.53) * mm});
            skLineSegment(sketch, "E28.MirrorCS", {"start": v(6240.08, -1336.08) * mm, "end": v(5263.95, -375.17) * mm});
            skLineSegment(sketch, "E29.MirrorCS", {"start": v(4919.85, -1700.98) * mm, "end": v(6240.08, -1336.08) * mm});
            skLineSegment(sketch, "E30", {"start": v(4276, 709.2) * mm, "end": v(4276, 0) * mm});
            skLineSegment(sketch, "E31", {"start": v(4276, 0) * mm, "end": v(4575.75, -375.17) * mm});
            skLineSegment(sketch, "E32.MirrorCS", {"start": v(5563.7, 709.2) * mm, "end": v(5563.7, 0) * mm});
            skLineSegment(sketch, "E33.MirrorCS", {"start": v(5563.7, 0) * mm, "end": v(5263.95, -375.17) * mm});
            skLineSegment(sketch, "E34.1.1", {"start": v(7564.72, -173.97) * mm, "end": v(7908.82, 1151.85) * mm});
            skLineSegment(sketch, "E34.1.2", {"start": v(6413.55, 1234.12) * mm, "end": v(6588.58, 786.94) * mm});
            skLineSegment(sketch, "E34.1.3", {"start": v(5769.7, 118.93) * mm, "end": v(6244.48, 190.94) * mm});
            skLineSegment(sketch, "E34.1.4", {"start": v(5155.51, 473.53) * mm, "end": v(4040.32, 1117.38) * mm});
            skLineSegment(sketch, "E34.1.5", {"start": v(4040.32, 1117.38) * mm, "end": v(4684.18, 2232.57) * mm});
            skLineSegment(sketch, "E34.1.6", {"start": v(5219.08, 782.96) * mm, "end": v(6244.48, 190.94) * mm});
            skLineSegment(sketch, "E34.1.7", {"start": v(4684.18, 2232.57) * mm, "end": v(5799.37, 1588.72) * mm});
            skLineSegment(sketch, "E34.1.8", {"start": v(4919.85, 1353.05) * mm, "end": v(7564.72, -173.97) * mm});
            skLineSegment(sketch, "E34.1.9", {"start": v(6244.48, 190.94) * mm, "end": v(7564.72, -173.97) * mm});
            skLineSegment(sketch, "E34.1.10", {"start": v(7564.72, -173.97) * mm, "end": v(6588.58, -1134.87) * mm});
            skPoint(sketch, "E34.1.11", {"position": v(5241.77, 1910.65) * mm});
            skPoint(sketch, "E34.1.12", {"position": v(7076.65, -654.42) * mm});
            skCircle(sketch, "E34.1.13", {"center": v(6799.26, -372.63) * mm, "radius": 395.4 * mm, "construction": true});
            skLineSegment(sketch, "E34.1.14", {"start": v(6588.58, -1134.87) * mm, "end": v(6244.48, 190.94) * mm});
            skLineSegment(sketch, "E34.1.15", {"start": v(5799.37, 1588.72) * mm, "end": v(6413.55, 1234.12) * mm});
            skLineSegment(sketch, "E34.1.16", {"start": v(7908.82, 1151.85) * mm, "end": v(6588.58, 786.94) * mm});
            skLineSegment(sketch, "E34.1.17", {"start": v(5155.51, 473.53) * mm, "end": v(5769.7, 118.93) * mm});
            skLineSegment(sketch, "E34.1.18", {"start": v(5799.37, 1588.72) * mm, "end": v(5155.51, 473.53) * mm});
            skLineSegment(sketch, "E34.1.19", {"start": v(5563.22, 1378.01) * mm, "end": v(6588.62, 786) * mm});
            skLineSegment(sketch, "E34.2.1", {"start": v(7564.72, 2880.07) * mm, "end": v(6588.58, 3840.98) * mm});
            skLineSegment(sketch, "E34.2.2", {"start": v(5769.7, 2587.17) * mm, "end": v(6244.48, 2515.16) * mm});
            skLineSegment(sketch, "E34.2.3", {"start": v(6413.55, 1471.98) * mm, "end": v(6588.58, 1919.16) * mm});
            skLineSegment(sketch, "E34.2.4", {"start": v(5799.37, 1117.38) * mm, "end": v(4684.18, 473.53) * mm});
            skLineSegment(sketch, "E34.2.5", {"start": v(4684.18, 473.53) * mm, "end": v(4040.32, 1588.72) * mm});
            skLineSegment(sketch, "E34.2.6", {"start": v(5563.18, 1327.15) * mm, "end": v(6588.58, 1919.16) * mm});
            skLineSegment(sketch, "E34.2.7", {"start": v(4040.32, 1588.72) * mm, "end": v(5155.51, 2232.57) * mm});
            skLineSegment(sketch, "E34.2.8", {"start": v(4919.85, 1353.05) * mm, "end": v(7564.72, 2880.07) * mm});
            skLineSegment(sketch, "E34.2.9", {"start": v(6588.58, 1919.16) * mm, "end": v(7564.72, 2880.07) * mm});
            skLineSegment(sketch, "E34.2.10", {"start": v(7564.72, 2880.07) * mm, "end": v(7908.82, 1554.26) * mm});
            skPoint(sketch, "E34.2.11", {"position": v(4597.92, 1910.65) * mm});
            skPoint(sketch, "E34.2.12", {"position": v(7736.77, 2217.16) * mm});
            skCircle(sketch, "E34.2.13", {"center": v(7354.04, 2117.83) * mm, "radius": 395.4 * mm, "construction": true});
            skLineSegment(sketch, "E34.2.14", {"start": v(7908.82, 1554.26) * mm, "end": v(6588.58, 1919.16) * mm});
            skLineSegment(sketch, "E34.2.15", {"start": v(5155.51, 2232.57) * mm, "end": v(5769.7, 2587.17) * mm});
            skLineSegment(sketch, "E34.2.16", {"start": v(6588.58, 3840.98) * mm, "end": v(6244.48, 2515.16) * mm});
            skLineSegment(sketch, "E34.2.17", {"start": v(5799.37, 1117.38) * mm, "end": v(6413.55, 1471.98) * mm});
            skLineSegment(sketch, "E34.2.18", {"start": v(5155.51, 2232.57) * mm, "end": v(5799.37, 1117.38) * mm});
            skLineSegment(sketch, "E34.2.19", {"start": v(5219.91, 1922.7) * mm, "end": v(6245.31, 2514.72) * mm});
            skLineSegment(sketch, "E34.3.1", {"start": v(4919.85, 4407.09) * mm, "end": v(3599.6, 4042.18) * mm});
            skLineSegment(sketch, "E34.3.2", {"start": v(4276, 2706.1) * mm, "end": v(4575.75, 3081.27) * mm});
            skLineSegment(sketch, "E34.3.3", {"start": v(5563.7, 2706.1) * mm, "end": v(5263.95, 3081.27) * mm});
            skLineSegment(sketch, "E34.3.6", {"start": v(5263.95, 1897.24) * mm, "end": v(5263.95, 3081.27) * mm});
            skLineSegment(sketch, "E34.3.8", {"start": v(4919.85, 1353.05) * mm, "end": v(4919.85, 4407.09) * mm});
            skLineSegment(sketch, "E34.3.9", {"start": v(5263.95, 3081.27) * mm, "end": v(4919.85, 4407.09) * mm});
            skLineSegment(sketch, "E34.3.10", {"start": v(4919.85, 4407.09) * mm, "end": v(6240.08, 4042.18) * mm});
            skPoint(sketch, "E34.3.11", {"position": v(4276, 1353.05) * mm});
            skPoint(sketch, "E34.3.12", {"position": v(5579.96, 4224.63) * mm});
            skCircle(sketch, "E34.3.13", {"center": v(5474.62, 3843.51) * mm, "radius": 395.4 * mm, "construction": true});
            skLineSegment(sketch, "E34.3.14", {"start": v(6240.08, 4042.18) * mm, "end": v(5263.95, 3081.27) * mm});
            skLineSegment(sketch, "E34.3.15", {"start": v(4276, 1996.9) * mm, "end": v(4276, 2706.1) * mm});
            skLineSegment(sketch, "E34.3.16", {"start": v(3599.6, 4042.18) * mm, "end": v(4575.75, 3081.27) * mm});
            skLineSegment(sketch, "E34.3.17", {"start": v(5563.7, 1996.9) * mm, "end": v(5563.7, 2706.1) * mm});
            skLineSegment(sketch, "E34.3.19", {"start": v(4576.54, 1897.75) * mm, "end": v(4576.54, 3081.77) * mm});
            skLineSegment(sketch, "E34.4.1", {"start": v(2274.97, 2880.07) * mm, "end": v(1930.87, 1554.26) * mm});
            skLineSegment(sketch, "E34.4.2", {"start": v(3426.14, 1471.98) * mm, "end": v(3251.11, 1919.16) * mm});
            skLineSegment(sketch, "E34.4.3", {"start": v(4070, 2587.17) * mm, "end": v(3595.21, 2515.16) * mm});
            skLineSegment(sketch, "E34.4.4", {"start": v(4684.18, 2232.57) * mm, "end": v(5799.37, 1588.72) * mm});
            skLineSegment(sketch, "E34.4.5", {"start": v(5799.37, 1588.72) * mm, "end": v(5155.51, 473.53) * mm});
            skLineSegment(sketch, "E34.4.6", {"start": v(4620.61, 1923.15) * mm, "end": v(3595.21, 2515.16) * mm});
            skLineSegment(sketch, "E34.4.7", {"start": v(5155.51, 473.53) * mm, "end": v(4040.32, 1117.38) * mm});
            skLineSegment(sketch, "E34.4.8", {"start": v(4919.85, 1353.05) * mm, "end": v(2274.97, 2880.07) * mm});
            skLineSegment(sketch, "E34.4.9", {"start": v(3595.21, 2515.16) * mm, "end": v(2274.97, 2880.07) * mm});
            skLineSegment(sketch, "E34.4.10", {"start": v(2274.97, 2880.07) * mm, "end": v(3251.11, 3840.98) * mm});
            skPoint(sketch, "E34.4.11", {"position": v(4597.92, 795.46) * mm});
            skPoint(sketch, "E34.4.12", {"position": v(2763.04, 3360.52) * mm});
            skCircle(sketch, "E34.4.13", {"center": v(3040.43, 3078.74) * mm, "radius": 395.4 * mm, "construction": true});
            skLineSegment(sketch, "E34.4.14", {"start": v(3251.11, 3840.98) * mm, "end": v(3595.21, 2515.16) * mm});
            skLineSegment(sketch, "E34.4.15", {"start": v(4040.32, 1117.38) * mm, "end": v(3426.14, 1471.98) * mm});
            skLineSegment(sketch, "E34.4.16", {"start": v(1930.87, 1554.26) * mm, "end": v(3251.11, 1919.16) * mm});
            skLineSegment(sketch, "E34.4.17", {"start": v(4684.18, 2232.57) * mm, "end": v(4070, 2587.17) * mm});
            skLineSegment(sketch, "E34.4.18", {"start": v(4040.32, 1117.38) * mm, "end": v(4684.18, 2232.57) * mm});
            skLineSegment(sketch, "E34.4.19", {"start": v(4276.47, 1328.09) * mm, "end": v(3251.08, 1920.1) * mm});
            skLineSegment(sketch, "E34.5.1", {"start": v(2274.97, -173.97) * mm, "end": v(3251.11, -1134.87) * mm});
            skLineSegment(sketch, "E34.5.2", {"start": v(4070, 118.93) * mm, "end": v(3595.21, 190.94) * mm});
            skLineSegment(sketch, "E34.5.3", {"start": v(3426.14, 1234.12) * mm, "end": v(3251.11, 786.94) * mm});
            skLineSegment(sketch, "E34.5.4", {"start": v(4040.32, 1588.72) * mm, "end": v(5155.51, 2232.57) * mm});
            skLineSegment(sketch, "E34.5.5", {"start": v(5155.51, 2232.57) * mm, "end": v(5799.37, 1117.38) * mm});
            skLineSegment(sketch, "E34.5.6", {"start": v(4276.51, 1378.95) * mm, "end": v(3251.11, 786.94) * mm});
            skLineSegment(sketch, "E34.5.7", {"start": v(5799.37, 1117.38) * mm, "end": v(4684.18, 473.53) * mm});
            skLineSegment(sketch, "E34.5.8", {"start": v(4919.85, 1353.05) * mm, "end": v(2274.97, -173.97) * mm});
            skLineSegment(sketch, "E34.5.9", {"start": v(3251.11, 786.94) * mm, "end": v(2274.97, -173.97) * mm});
            skLineSegment(sketch, "E34.5.10", {"start": v(2274.97, -173.97) * mm, "end": v(1930.87, 1151.85) * mm});
            skPoint(sketch, "E34.5.11", {"position": v(5241.77, 795.46) * mm});
            skPoint(sketch, "E34.5.12", {"position": v(2102.92, 488.94) * mm});
            skCircle(sketch, "E34.5.13", {"center": v(2485.65, 588.27) * mm, "radius": 395.4 * mm, "construction": true});
            skLineSegment(sketch, "E34.5.14", {"start": v(1930.87, 1151.85) * mm, "end": v(3251.11, 786.94) * mm});
            skLineSegment(sketch, "E34.5.15", {"start": v(4684.18, 473.53) * mm, "end": v(4070, 118.93) * mm});
            skLineSegment(sketch, "E34.5.16", {"start": v(3251.11, -1134.87) * mm, "end": v(3595.21, 190.94) * mm});
            skLineSegment(sketch, "E34.5.17", {"start": v(4040.32, 1588.72) * mm, "end": v(3426.14, 1234.12) * mm});
            skLineSegment(sketch, "E34.5.18", {"start": v(4684.18, 473.53) * mm, "end": v(4040.32, 1588.72) * mm});
            skLineSegment(sketch, "E34.5.19", {"start": v(4619.78, 783.4) * mm, "end": v(3594.38, 191.38) * mm});
            skSolve(sketch);
        }
        {
            var Q0;
            Q0 = qSketchRegion(id + "F0", true);
            extrude(context, id + "F1", {"entities" : qUnion([Q0]), "depth" : 600 * mm, "offsetDistance" : 25 * mm});
        }
    });
